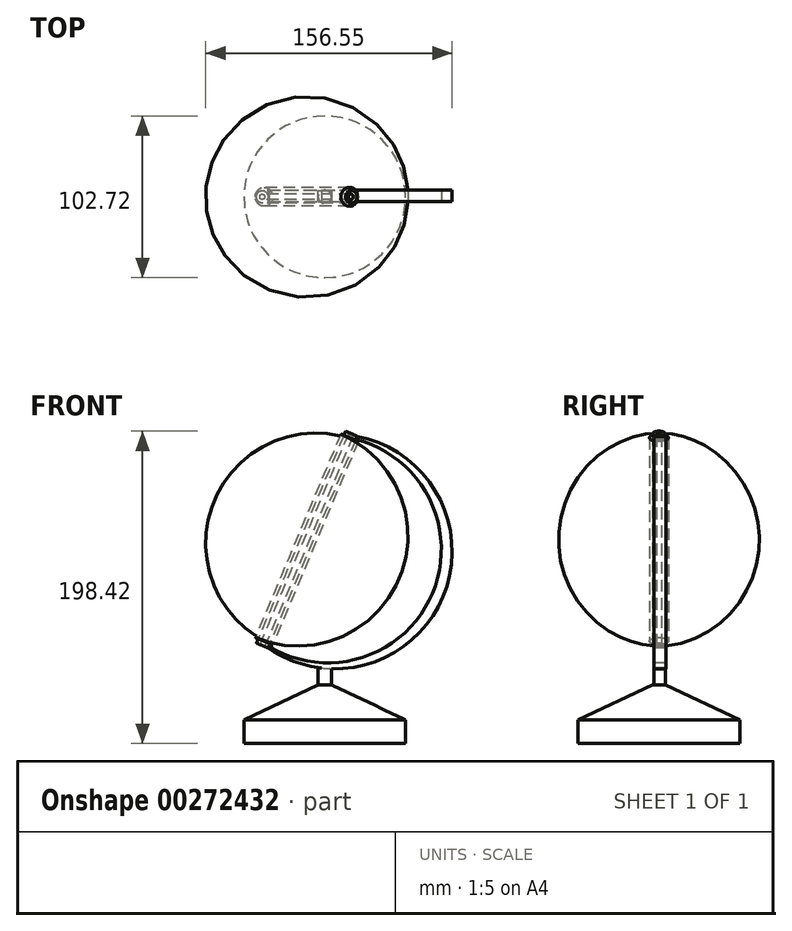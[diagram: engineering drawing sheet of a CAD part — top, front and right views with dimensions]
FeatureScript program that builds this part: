
annotation { "Feature Type Name" : "Feature", "Feature Type Description" : "" }
export const myFeature = defineFeature(function(context is Context, id is Id, definition is map)
    precondition{}
    {
        {
            var Q0;
            Q0=qCreatedBy(makeId("Front.planeOp"),FACE);
            var sketch = newSketch(context, id + "F0", { "sketchPlane" : qUnion([Q0])});
            skLineSegment(sketch, "E0", {"start": v(3.94, -68.49) * mm, "end": v(58.24, 60.72) * mm});
            skArc(sketch, "E1", {"start": v(3.94, -68.49) * mm, "mid": v(95.97, -31.15) * mm, "end": v(58.24, 60.72) * mm});
            skLineSegment(sketch, "E2", {"start": v(51.71, 60.72) * mm, "end": v(-1.98, -67.02) * mm, "construction": true});
            skLineSegment(sketch, "E3", {"start": v(-1.2, -69.55) * mm, "end": v(55.01, 64.19) * mm});
            skLineSegment(sketch, "E4", {"start": v(-1.2, -69.55) * mm, "end": v(0.92, -70.43) * mm});
            skLineSegment(sketch, "E5", {"start": v(0.92, -70.43) * mm, "end": v(57.5, 64.19) * mm});
            skLineSegment(sketch, "E6", {"start": v(57.5, 64.19) * mm, "end": v(55.01, 64.19) * mm});
            skSolve(sketch);
        }
        {
            var Q0;
            Q0=sQuery(id+"F0.wireOp",EDGE,"E0");
            var Q1;
            Q1=sQuery(id+"F0.wireOp",EDGE,"E1");
            var Q2;
            Q2=sQuery(id+"F0.wireOp",EDGE,"E2");
            revolve(context, id + "F1", {"bodyType" : ToolBodyType.SURFACE, "surfaceEntities" : qUnion([Q0, Q1]), "axis" : qUnion([Q2]), "revolveType" : RevolveType.FULL});
        }
        {
            var Q0;
            Q0=qCreatedBy(makeId("Front.planeOp"),FACE);
            var sketch = newSketch(context, id + "F2", { "sketchPlane" : qUnion([Q0])});
            skSolve(sketch);
        }
        {
            var Q0;
            Q0 = qSketchRegion(id + "F0", true);
            var Q1;
            Q1=makeQuery(id+"F1.opRevolve","SWEPT_FACE",FACE,{"disambiguationData":[OSD([sQuery(id+"F0.wireOp",EDGE,"E1")])]});
            revolve(context, id + "F3", {"entities" : qUnion([Q0]), "axis" : qUnion([Q1]), "revolveType" : RevolveType.FULL});
        }
        {
            var Q0;
            Q0=qCreatedBy(makeId("Front.planeOp"),FACE);
            var sketch = newSketch(context, id + "F4", { "sketchPlane" : qUnion([Q0])});
            skArc(sketch, "E7", {"start": v(0.98, -70.46) * mm, "mid": v(112, -37.97) * mm, "end": v(57.5, 64.06) * mm});
            skArc(sketch, "E8", {"start": v(1.39, -69.33) * mm, "mid": v(105.34, -35.7) * mm, "end": v(56.6, 62.1) * mm});
            skLineSegment(sketch, "E9", {"start": v(1.39, -69.33) * mm, "end": v(0.98, -70.46) * mm});
            skLineSegment(sketch, "E10", {"start": v(57.5, 64.06) * mm, "end": v(56.6, 62.1) * mm});
            skSolve(sketch);
        }
        {
            var Q0;
            Q0=makeQuery(id+"F4.imprint","IMPRINT",FACE,{"disambiguationData":[TD([[makeQuery(id+"F4.imprint","IMPRINT",EDGE,{"derivedFrom":sQuery(id+"F4.wireOp",EDGE,"E7")}),1.0]])]});
            extrude(context, id + "F5", {"entities" : qUnion([Q0]), "operationType" : NewBodyOperationType.ADD, "oppositeDirection" : true, "depth" : 4.32 * mm, "hasSecondDirection" : true, "secondDirectionOppositeDirection" : false, "secondDirectionDepth" : 3.05 * mm});
        }
        {
            var Q0;
            Q0=qCreatedBy(makeId("Front.planeOp"),FACE);
            var sketch = newSketch(context, id + "F6", { "sketchPlane" : qUnion([Q0])});
            skLineSegment(sketch, "E11.bottom", {"start": v(32.76, -83.16) * mm, "end": v(41.12, -83.16) * mm});
            skLineSegment(sketch, "E11.top", {"start": v(32.76, -93.92) * mm, "end": v(41.12, -93.92) * mm});
            skLineSegment(sketch, "E11.left", {"start": v(32.76, -83.16) * mm, "end": v(32.76, -93.92) * mm});
            skLineSegment(sketch, "E11.right", {"start": v(41.12, -83.16) * mm, "end": v(41.12, -93.92) * mm});
            skLineSegment(sketch, "E12", {"start": v(36.94, -93.92) * mm, "end": v(36.94, -131.14) * mm});
            skLineSegment(sketch, "E13", {"start": v(36.94, -131.14) * mm, "end": v(88.3, -131.14) * mm});
            skLineSegment(sketch, "E14", {"start": v(88.3, -131.14) * mm, "end": v(88.3, -116.03) * mm});
            skLineSegment(sketch, "E15", {"start": v(88.3, -116.03) * mm, "end": v(41.12, -93.92) * mm});
            skSolve(sketch);
        }
        {
            var Q0;
            Q0=makeQuery(id+"F6.imprint","IMPRINT",FACE,{"disambiguationData":[TD([[makeQuery(id+"F6.imprint","IMPRINT",EDGE,{"derivedFrom":sQuery(id+"F6.wireOp",EDGE,"E11.bottom")}),-1.0]])]});
            extrude(context, id + "F7", {"entities" : qUnion([Q0]), "operationType" : NewBodyOperationType.ADD, "depth" : 3.05 * mm, "hasSecondDirection" : true, "secondDirectionOppositeDirection" : true, "secondDirectionDepth" : 4.06 * mm});
        }
        {
            var Q0;
            {var subQ0=sQuery(id+"F6.wireOp",EDGE,"E12");Q0=makeQuery(id+"F6.imprint","IMPRINT",FACE,{"disambiguationData":[TD([[makeQuery(id+"F6.imprint","IMPRINT",EDGE,{"derivedFrom":subQ0}),1.0]])]});}
            var Q1;
            Q1=sQuery(id+"F6.wireOp",EDGE,"E12");
            revolve(context, id + "F8", {"entities" : qUnion([Q0]), "axis" : qUnion([Q1]), "revolveType" : RevolveType.FULL});
        }
    });
